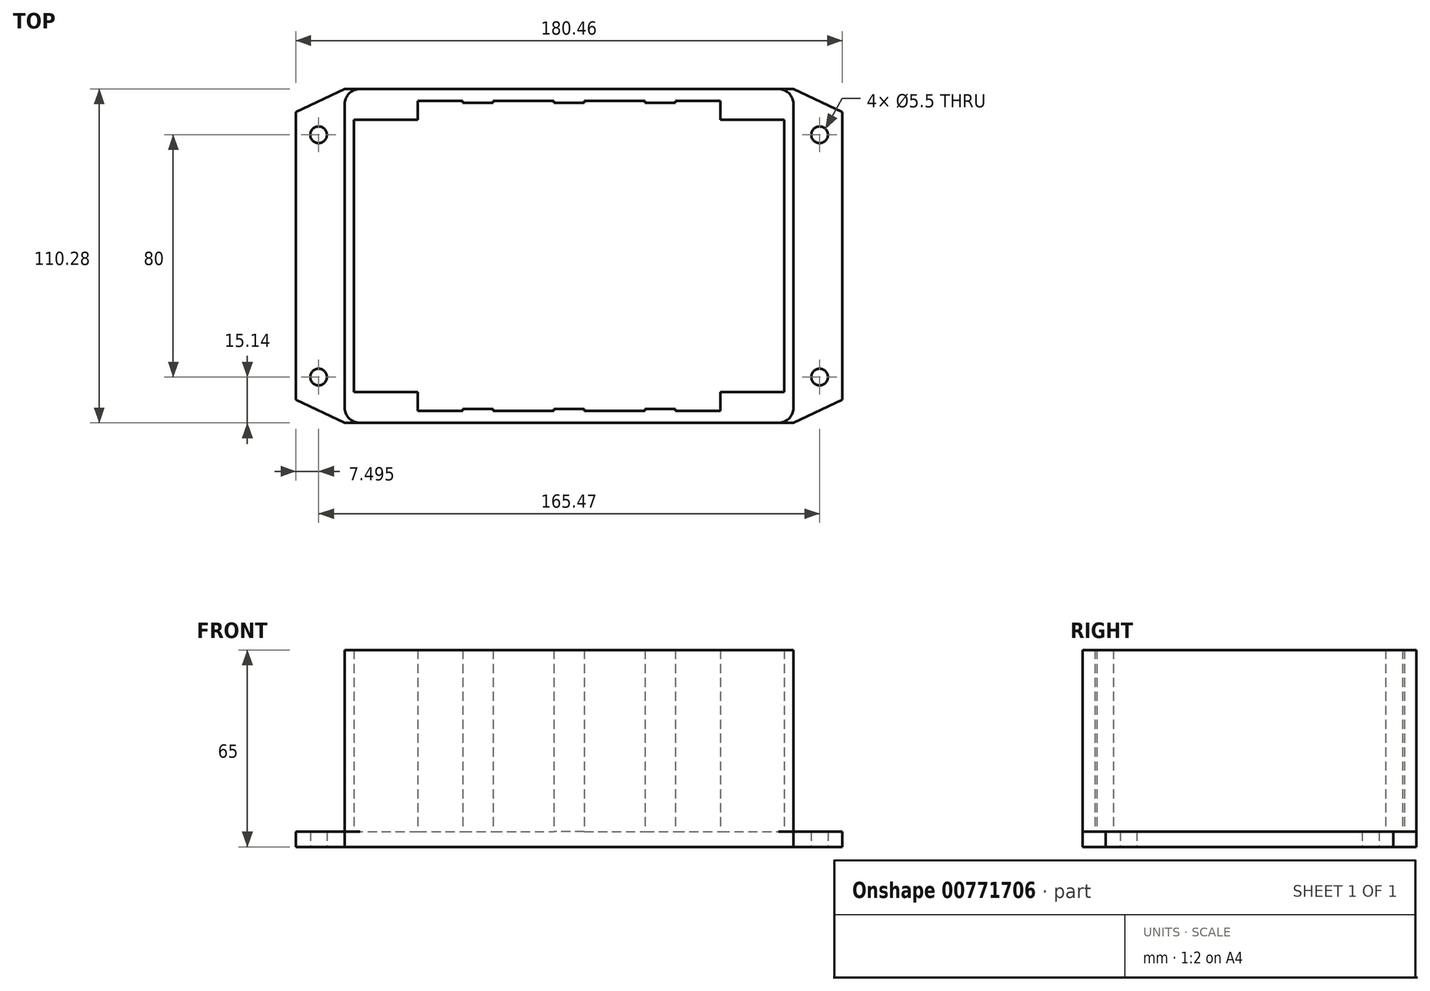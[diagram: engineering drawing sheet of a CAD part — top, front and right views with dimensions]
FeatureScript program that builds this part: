
annotation { "Feature Type Name" : "Feature", "Feature Type Description" : "" }
export const myFeature = defineFeature(function(context is Context, id is Id, definition is map)
    precondition{}
    {
        {
            var Q0;
            Q0=qCreatedBy(makeId("Top.planeOp"),FACE);
            var sketch = newSketch(context, id + "F0", { "sketchPlane" : qUnion([Q0])});
            skLineSegment(sketch, "E0", {"start": v(-74.1, 55.14) * mm, "end": v(74.1, 55.14) * mm});
            skLineSegment(sketch, "E1", {"start": v(74.1, 55.14) * mm, "end": v(90.23, 47.5) * mm});
            skLineSegment(sketch, "E2", {"start": v(90.23, 47.5) * mm, "end": v(90.23, -47.5) * mm});
            skLineSegment(sketch, "E3", {"start": v(90.23, -47.5) * mm, "end": v(74.1, -55.13) * mm});
            skLineSegment(sketch, "E4", {"start": v(74.1, -55.13) * mm, "end": v(-74.1, -55.14) * mm});
            skLineSegment(sketch, "E5", {"start": v(0, 0) * mm, "end": v(-154.52, 0) * mm, "construction": true});
            skLineSegment(sketch, "E6", {"start": v(0, 0) * mm, "end": v(0, 90.96) * mm, "construction": true});
            skLineSegment(sketch, "E7", {"start": v(-74.1, 55.14) * mm, "end": v(-90.23, 47.5) * mm});
            skLineSegment(sketch, "E8", {"start": v(-90.23, 47.5) * mm, "end": v(-90.23, -47.5) * mm});
            skLineSegment(sketch, "E9", {"start": v(-90.23, -47.5) * mm, "end": v(-74.1, -55.13) * mm});
            skCircle(sketch, "E10", {"center": v(-82.74, 40) * mm, "radius": 2.75 * mm});
            skCircle(sketch, "E11", {"center": v(82.74, 40) * mm, "radius": 2.75 * mm});
            skCircle(sketch, "E12", {"center": v(82.74, -40) * mm, "radius": 2.75 * mm});
            skCircle(sketch, "E13", {"center": v(-82.73, -40) * mm, "radius": 2.75 * mm});
            skSolve(sketch);
        }
        {
            var Q0;
            Q0=makeQuery(id+"F0.imprint","IMPRINT",FACE,{"disambiguationData":[TD([[makeQuery(id+"F0.imprint","IMPRINT",EDGE,{"derivedFrom":sQuery(id+"F0.wireOp",EDGE,"E0")}),-1.0]])]});
            extrude(context, id + "F1", {"entities" : qUnion([Q0]), "depth" : 5 * mm, "offsetDistance" : 25 * mm});
        }
        {
            var Q0;
            Q0=makeQuery(id+"F1.opExtrude","CAP_FACE",FACE,{"disambiguationData":[OSD([sQuery(id+"F0.wireOp",EDGE,"E0"),sQuery(id+"F0.wireOp",EDGE,"E1"),sQuery(id+"F0.wireOp",EDGE,"E2"),sQuery(id+"F0.wireOp",EDGE,"E3"),sQuery(id+"F0.wireOp",EDGE,"E4"),sQuery(id+"F0.wireOp",EDGE,"E7"),sQuery(id+"F0.wireOp",EDGE,"E8"),sQuery(id+"F0.wireOp",EDGE,"E9"),sQuery(id+"F0.wireOp",EDGE,"E10"),sQuery(id+"F0.wireOp",EDGE,"E11"),sQuery(id+"F0.wireOp",EDGE,"E12"),sQuery(id+"F0.wireOp",EDGE,"E13")])],"isStart":false});
            var sketch = newSketch(context, id + "F2", { "sketchPlane" : qUnion([Q0])});
            skLineSegment(sketch, "E14.bottom", {"start": v(69.1, 55.14) * mm, "end": v(-69.1, 55.14) * mm});
            skLineSegment(sketch, "E14.top", {"start": v(69.1, -55.14) * mm, "end": v(-69.1, -55.14) * mm});
            skLineSegment(sketch, "E14.left", {"start": v(74.1, 50.14) * mm, "end": v(74.1, -50.14) * mm});
            skLineSegment(sketch, "E14.right", {"start": v(-74.1, 50.14) * mm, "end": v(-74.1, -50.14) * mm});
            skPoint(sketch, "E14.middle", {"position": v(0, 0) * mm});
            skPoint(sketch, "E15.visualSharp", {"position": v(-74.1, 55.14) * mm});
            skArc(sketch, "E15.filletArc", {"start": v(-69.1, 55.14) * mm, "mid": v(-72.64, 53.67) * mm, "end": v(-74.1, 50.14) * mm});
            skPoint(sketch, "E16.visualSharp", {"position": v(74.1, 55.14) * mm});
            skArc(sketch, "E16.filletArc", {"start": v(74.1, 50.14) * mm, "mid": v(72.64, 53.67) * mm, "end": v(69.1, 55.14) * mm});
            skPoint(sketch, "E17.visualSharp", {"position": v(74.1, -55.14) * mm});
            skArc(sketch, "E17.filletArc", {"start": v(69.1, -55.14) * mm, "mid": v(72.64, -53.67) * mm, "end": v(74.1, -50.14) * mm});
            skPoint(sketch, "E18.visualSharp", {"position": v(-74.1, -55.14) * mm});
            skArc(sketch, "E18.filletArc", {"start": v(-74.1, -50.14) * mm, "mid": v(-72.64, -53.67) * mm, "end": v(-69.1, -55.14) * mm});
            skLineSegment(sketch, "E19", {"start": v(0, 50.5) * mm, "end": v(-5, 50.5) * mm});
            skLineSegment(sketch, "E20", {"start": v(-5, 50.5) * mm, "end": v(-5, 51.14) * mm});
            skLineSegment(sketch, "E21", {"start": v(-5, 51.14) * mm, "end": v(-25.1, 51.14) * mm});
            skLineSegment(sketch, "E22", {"start": v(-25.1, 51.14) * mm, "end": v(-25.1, 50.5) * mm});
            skLineSegment(sketch, "E23", {"start": v(-25.1, 50.5) * mm, "end": v(-35.1, 50.5) * mm});
            skLineSegment(sketch, "E24", {"start": v(-35.1, 50.5) * mm, "end": v(-35.1, 51.14) * mm});
            skLineSegment(sketch, "E25", {"start": v(-35.1, 51.14) * mm, "end": v(-50, 51.14) * mm});
            skLineSegment(sketch, "E26", {"start": v(-50, 51.14) * mm, "end": v(-50, 45) * mm});
            skLineSegment(sketch, "E27", {"start": v(-50, 45) * mm, "end": v(-71.1, 45) * mm});
            skLineSegment(sketch, "E28", {"start": v(-71.1, 45) * mm, "end": v(-71.1, -45) * mm});
            skLineSegment(sketch, "E29", {"start": v(-71.1, -45) * mm, "end": v(-50, -45) * mm});
            skLineSegment(sketch, "E30", {"start": v(-50, -45) * mm, "end": v(-50, -51.14) * mm});
            skLineSegment(sketch, "E31", {"start": v(-50, -51.14) * mm, "end": v(-35.1, -51.14) * mm});
            skLineSegment(sketch, "E32", {"start": v(-35.1, -51.14) * mm, "end": v(-35.1, -50.5) * mm});
            skLineSegment(sketch, "E33", {"start": v(-35.1, -50.5) * mm, "end": v(-25.1, -50.5) * mm});
            skLineSegment(sketch, "E34", {"start": v(-25.1, -50.5) * mm, "end": v(-25.1, -51.14) * mm});
            skLineSegment(sketch, "E35", {"start": v(-25.1, -51.14) * mm, "end": v(-5, -51.14) * mm});
            skLineSegment(sketch, "E36", {"start": v(-5, -51.14) * mm, "end": v(-5, -50.5) * mm});
            skLineSegment(sketch, "E37", {"start": v(-5, -50.5) * mm, "end": v(0, -50.5) * mm});
            skLineSegment(sketch, "E38", {"start": v(0, 0) * mm, "end": v(-57.29, 0) * mm, "construction": true});
            skLineSegment(sketch, "E39", {"start": v(0, -22.06) * mm, "end": v(0, 27.09) * mm, "construction": true});
            skLineSegment(sketch, "E40.MirrorCS", {"start": v(0, 50.5) * mm, "end": v(5, 50.5) * mm});
            skLineSegment(sketch, "E41.MirrorCS", {"start": v(5, 50.5) * mm, "end": v(5, 51.14) * mm});
            skLineSegment(sketch, "E42.MirrorCS", {"start": v(5, 51.14) * mm, "end": v(25.1, 51.14) * mm});
            skLineSegment(sketch, "E43.MirrorCS", {"start": v(25.1, 51.14) * mm, "end": v(25.1, 50.5) * mm});
            skLineSegment(sketch, "E44.MirrorCS", {"start": v(25.1, 50.5) * mm, "end": v(35.1, 50.5) * mm});
            skLineSegment(sketch, "E45.MirrorCS", {"start": v(35.1, 51.14) * mm, "end": v(50, 51.14) * mm});
            skLineSegment(sketch, "E46.MirrorCS", {"start": v(50, 51.14) * mm, "end": v(50, 45) * mm});
            skLineSegment(sketch, "E47.MirrorCS", {"start": v(35.1, 50.5) * mm, "end": v(35.1, 51.14) * mm});
            skLineSegment(sketch, "E48.MirrorCS", {"start": v(50, 45) * mm, "end": v(71.1, 45) * mm});
            skLineSegment(sketch, "E49.MirrorCS", {"start": v(71.1, 45) * mm, "end": v(71.1, -45) * mm});
            skLineSegment(sketch, "E50.MirrorCS", {"start": v(71.1, -45) * mm, "end": v(50, -45) * mm});
            skLineSegment(sketch, "E51.MirrorCS", {"start": v(50, -45) * mm, "end": v(50, -51.14) * mm});
            skLineSegment(sketch, "E52.MirrorCS", {"start": v(50, -51.14) * mm, "end": v(35.1, -51.14) * mm});
            skLineSegment(sketch, "E53.MirrorCS", {"start": v(35.1, -50.5) * mm, "end": v(25.1, -50.5) * mm});
            skLineSegment(sketch, "E54.MirrorCS", {"start": v(25.1, -51.14) * mm, "end": v(5, -51.14) * mm});
            skLineSegment(sketch, "E55.MirrorCS", {"start": v(5, -50.5) * mm, "end": v(0, -50.5) * mm});
            skLineSegment(sketch, "E56.MirrorCS", {"start": v(5, -51.14) * mm, "end": v(5, -50.5) * mm});
            skLineSegment(sketch, "E57.MirrorCS", {"start": v(35.1, -51.14) * mm, "end": v(35.1, -50.5) * mm});
            skLineSegment(sketch, "E58.MirrorCS", {"start": v(25.1, -50.5) * mm, "end": v(25.1, -51.14) * mm});
            skSolve(sketch);
        }
        {
            var Q0;
            Q0=makeQuery(id+"F2.imprint","IMPRINT",FACE,{"disambiguationData":[TD([[makeQuery(id+"F2.imprint","IMPRINT",EDGE,{"derivedFrom":sQuery(id+"F2.wireOp",EDGE,"E14.bottom")}),-1.0]])]});
            extrude(context, id + "F3", {"entities" : qUnion([Q0]), "operationType" : NewBodyOperationType.ADD, "depth" : 60 * mm, "offsetDistance" : 25 * mm});
        }
    });
